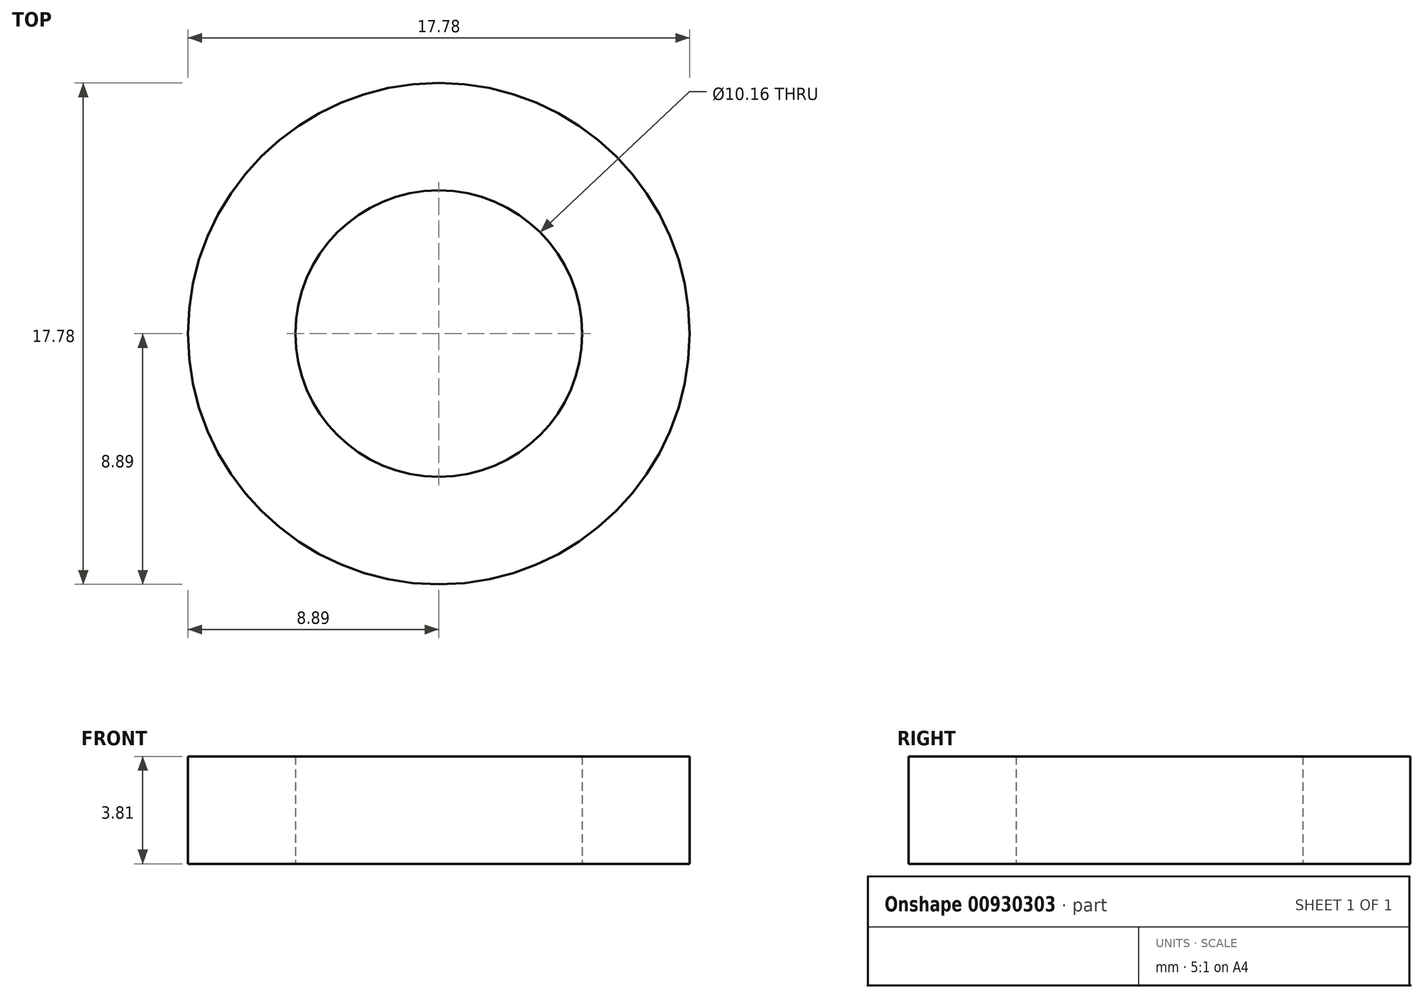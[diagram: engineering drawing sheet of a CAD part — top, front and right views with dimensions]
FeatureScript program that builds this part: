
annotation { "Feature Type Name" : "Feature", "Feature Type Description" : "" }
export const myFeature = defineFeature(function(context is Context, id is Id, definition is map)
    precondition{}
    {
        {
            var Q0;
            Q0=qCreatedBy(makeId("Top.planeOp"),FACE);
            var sketch = newSketch(context, id + "F0", { "sketchPlane" : qUnion([Q0])});
            skCircle(sketch, "E0", {"center": v(0, 0) * mm, "radius": 8.9 * mm});
            skCircle(sketch, "E1", {"center": v(0, 0) * mm, "radius": 5.08 * mm});
            skSolve(sketch);
        }
        {
            var Q0;
            Q0 = qSketchRegion(id + "F0", true);
            extrude(context, id + "F1", {"entities" : qUnion([Q0]), "depth" : 3.8 * mm, "offsetDistance" : 25.4 * mm});
        }
    });
